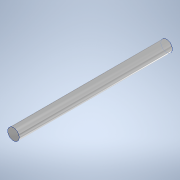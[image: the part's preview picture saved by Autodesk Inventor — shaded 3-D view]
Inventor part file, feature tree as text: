
AUTODESK INVENTOR PART (.ipt)
format: ipt  version: 2020.3 (Build 243373000, 373)  size: 94,720 bytes
history: native  units: mm
features: other x1, extrude x1, sketch x1
ambient origin geometry x8: Origin, YZ Plane, XZ Plane, XY Plane, X Axis, Y Axis, Z Axis, Center Point
bodies: Body1 (feature_tree)
feature tree (3):
  other  "ソリッド1"
  extrude  "押し出し1"  Depth=6.0mm
  sketch  "スケッチ1"
